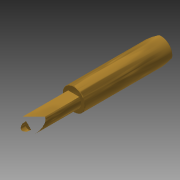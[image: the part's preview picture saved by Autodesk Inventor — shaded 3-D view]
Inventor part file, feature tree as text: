
AUTODESK INVENTOR PART (.ipt)
format: ipt  version: 2014 (Build 180170000, 170)  size: 103,424 bytes
history: native  units: mm (DEFAULTED — no unit token found)
features: extrude x3, sketch x3, chamfer x1
ambient origin geometry x8: Origin, YZ Plane, XZ Plane, XY Plane, X Axis, Y Axis, Z Axis, Center Point
bodies: Solid1 (feature_tree)
feature tree (7):
  extrude  "Extrusion1"  Depth=45.24375mm
  extrude  "Extrusion2"  Depth=17.4625mm
  extrude  "Extrusion3"  Depth=3.175mm
  chamfer  "Chamfer1"  Distance=7.14375mm
  sketch  "Sketch1"  dims[d0=45.24375mm d1=0.0mm d2=4.7625mm]
  sketch  "Sketch2"  dims[d3=17.4625mm d4=0.0mm d5=2.286mm]
  sketch  "Sketch3"  dims[d6=3.175mm d7=0.0mm d8=0.127mm d9=0.127mm d10=7.14375mm d11=45.0deg]
